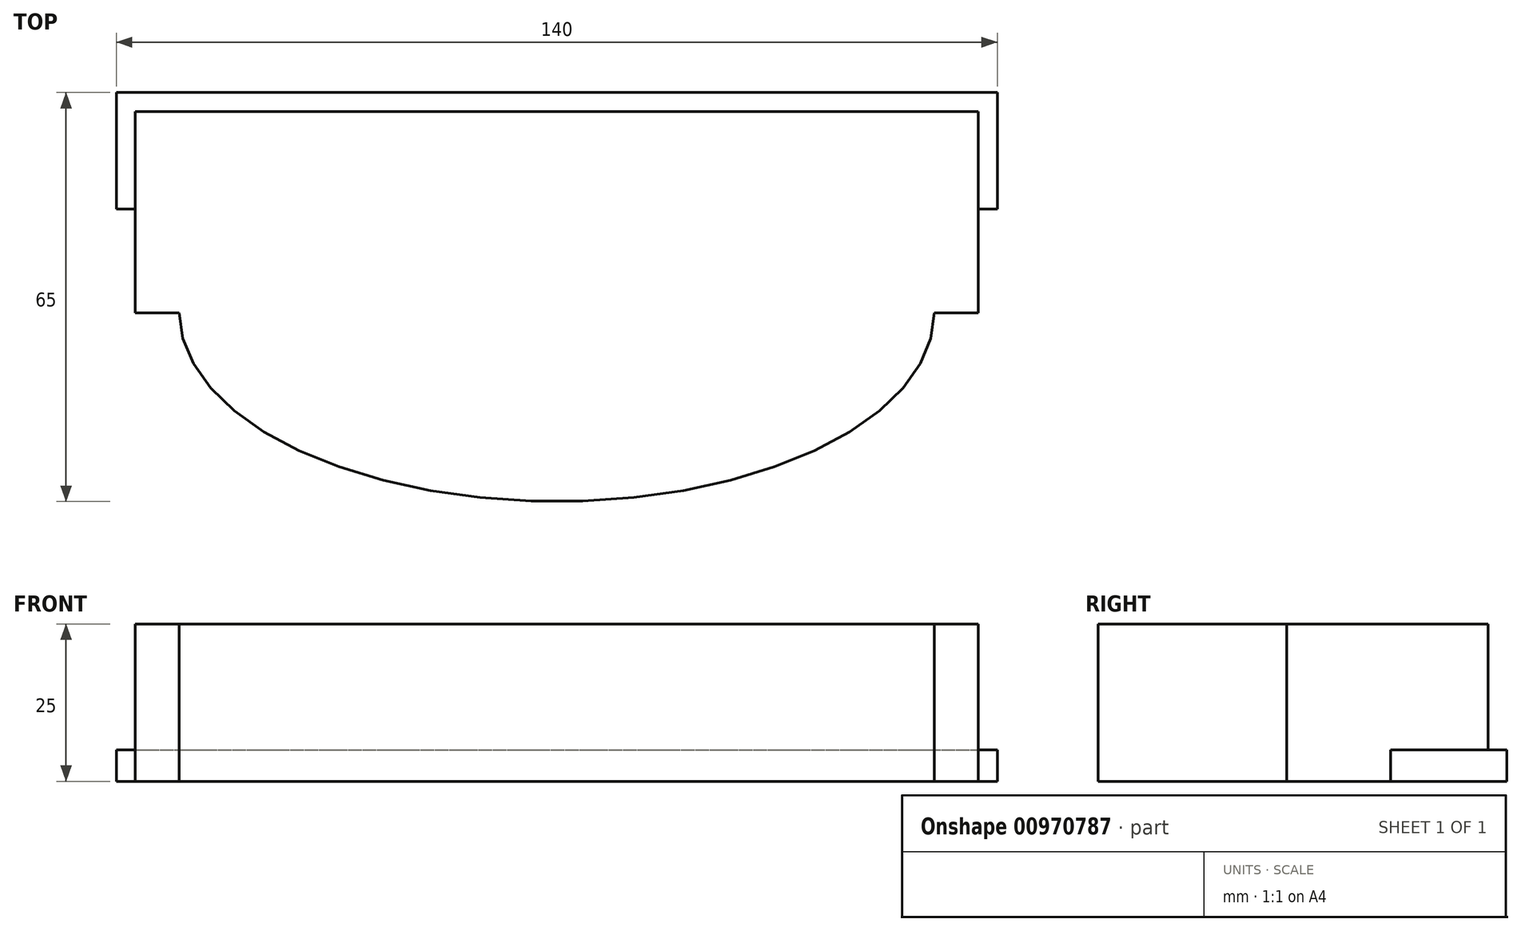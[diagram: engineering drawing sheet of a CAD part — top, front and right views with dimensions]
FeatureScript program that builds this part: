
annotation { "Feature Type Name" : "Feature", "Feature Type Description" : "" }
export const myFeature = defineFeature(function(context is Context, id is Id, definition is map)
    precondition{}
    {
        {
            var Q0;
            Q0=qCreatedBy(makeId("Top.planeOp"),FACE);
            var sketch = newSketch(context, id + "F0", { "sketchPlane" : qUnion([Q0])});
            skEllipticalArc(sketch, "E0", {});
            skPoint(sketch, "E1.middle", {"position": v(-166.82, 0) * mm});
            skLineSegment(sketch, "E2", {"start": v(-70, 0) * mm, "end": v(-70, 35) * mm});
            skLineSegment(sketch, "E3", {"start": v(0, 35) * mm, "end": v(-70, 35) * mm});
            skLineSegment(sketch, "E4", {"start": v(70, 0) * mm, "end": v(70, 35) * mm});
            skLineSegment(sketch, "E5", {"start": v(0, 35) * mm, "end": v(70, 35) * mm});
            skLineSegment(sketch, "E6", {"start": v(67, 0) * mm, "end": v(60, 0) * mm});
            skLineSegment(sketch, "E7", {"start": v(-67, 0) * mm, "end": v(-60, 0) * mm});
            skPoint(sketch, "E1.left.end.orphan", {"position": v(-134.32, 15) * mm});
            skPoint(sketch, "E1.bottom.start.orphan", {"position": v(-134.32, -15) * mm});
            skPoint(sketch, "E1.right.end.orphan", {"position": v(-199.32, 15) * mm});
            skPoint(sketch, "E1.right.start.orphan", {"position": v(-199.32, -15) * mm});
            skPoint(sketch, "E8.middle", {"position": v(-278.18, 48.93) * mm});
            skLineSegment(sketch, "E9", {"start": v(-67, 32) * mm, "end": v(-67, 0) * mm});
            skLineSegment(sketch, "E10", {"start": v(70, 32) * mm, "end": v(67, 32) * mm});
            skPoint(sketch, "E11.endSnap0", {"position": v(35, 35) * mm});
            skLineSegment(sketch, "E12", {"start": v(-67, 32) * mm, "end": v(67, 32) * mm});
            skLineSegment(sketch, "E13", {"start": v(67, 32) * mm, "end": v(67, 0) * mm});
            skPoint(sketch, "E11.end.orphan", {"position": v(67, 35) * mm});
            skPoint(sketch, "E8.right.end.orphan", {"position": v(-310.68, 63.93) * mm});
            skPoint(sketch, "E8.right.start.orphan", {"position": v(-310.68, 33.93) * mm});
            skPoint(sketch, "E8.left.end.orphan", {"position": v(-245.68, 63.93) * mm});
            skPoint(sketch, "E8.left.start.orphan", {"position": v(-245.68, 33.93) * mm});
            skLineSegment(sketch, "E14.bottom", {"start": v(-67, 32) * mm, "end": v(-2, 32) * mm});
            skLineSegment(sketch, "E14.top", {"start": v(-67, 2) * mm, "end": v(-2, 2) * mm});
            skLineSegment(sketch, "E14.left", {"start": v(-67, 32) * mm, "end": v(-67, 2) * mm});
            skLineSegment(sketch, "E14.right", {"start": v(-2, 32) * mm, "end": v(-2, 2) * mm});
            const initialGuessF0  = {"E0": [0, 0, 1, 0, 0.07, 0.035, 3.141592653589793, 0], "E0": [0, 0, 1, 0, 0.06, 0.03, 3.141592653589793, 0]};
            skSetInitialGuess(sketch, initialGuessF0);
            skSolve(sketch);
        }
        {
            var Q0;
            Q0 = qSketchRegion(id + "F0", true);
            extrude(context, id + "F1", {"entities" : qUnion([Q0]), "depth" : 25 * mm, "offsetDistance" : 25 * mm});
        }
        {
            var Q0;
            Q0=qCreatedBy(makeId("Top.planeOp"),FACE);
            var sketch = newSketch(context, id + "F2", { "sketchPlane" : qUnion([Q0])});
            skPoint(sketch, "E15.start.orphan", {"position": v(0, 0) * mm});
            skPoint(sketch, "E16.start.orphan", {"position": v(-63.94, 0) * mm});
            skLineSegment(sketch, "E17", {"start": v(0, 0) * mm, "end": v(0, 16.5) * mm});
            skLineSegment(sketch, "E18", {"start": v(0, 16.5) * mm, "end": v(-70, 16.5) * mm});
            skLineSegment(sketch, "E19", {"start": v(0, 16.5) * mm, "end": v(70, 16.5) * mm});
            skLineSegment(sketch, "E20", {"start": v(-70, 16.5) * mm, "end": v(-70, 35) * mm});
            skLineSegment(sketch, "E21", {"start": v(70, 16.5) * mm, "end": v(70, 35) * mm});
            skLineSegment(sketch, "E22", {"start": v(-70, 35) * mm, "end": v(70, 35) * mm});
            skSolve(sketch);
        }
        {
            var Q0;
            Q0 = qSketchRegion(id + "F2", true);
            extrude(context, id + "F3", {"entities" : qUnion([Q0]), "operationType" : NewBodyOperationType.ADD, "depth" : 5 * mm, "offsetDistance" : 25 * mm});
        }
    });
